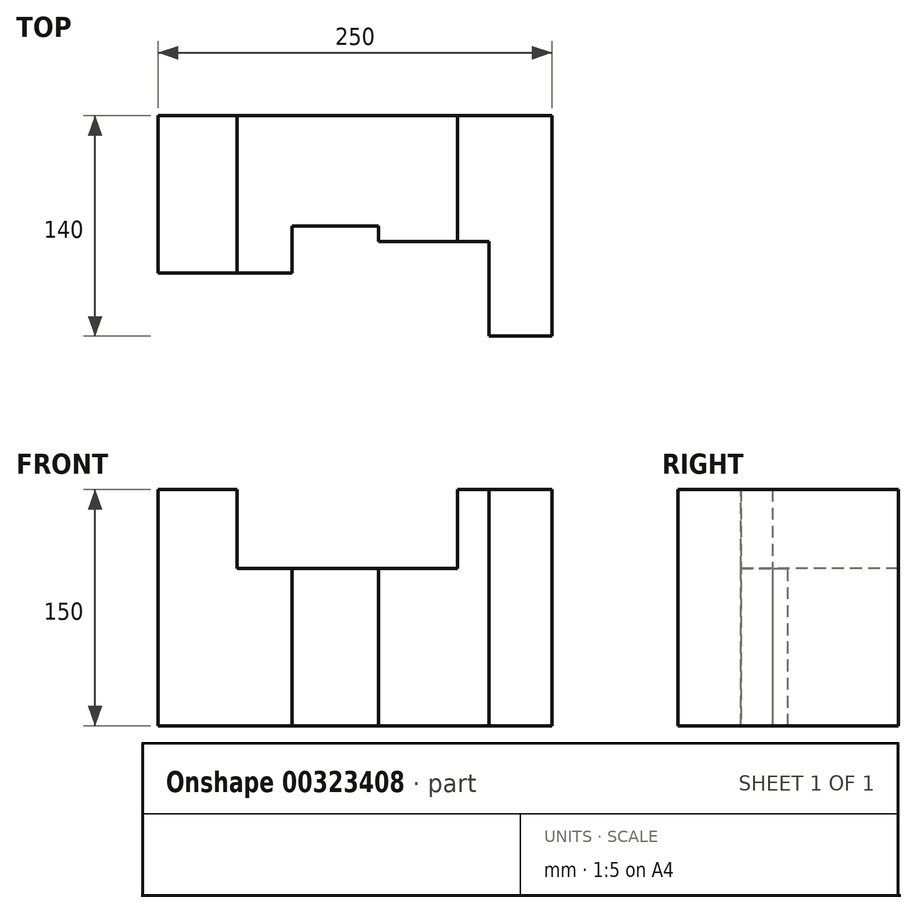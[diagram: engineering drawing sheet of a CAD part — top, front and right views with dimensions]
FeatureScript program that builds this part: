
annotation { "Feature Type Name" : "Feature", "Feature Type Description" : "" }
export const myFeature = defineFeature(function(context is Context, id is Id, definition is map)
    precondition{}
    {
        {
            var Q0;
            Q0=qCreatedBy(makeId("Front.planeOp"),FACE);
            var sketch = newSketch(context, id + "F0", { "sketchPlane" : qUnion([Q0])});
            skLineSegment(sketch, "E0.bottom", {"start": v(0, 0) * mm, "end": v(250, 0) * mm});
            skLineSegment(sketch, "E0.top", {"start": v(0, 150) * mm, "end": v(250, 150) * mm});
            skLineSegment(sketch, "E0.left", {"start": v(0, 0) * mm, "end": v(0, 150) * mm});
            skLineSegment(sketch, "E0.right", {"start": v(250, 0) * mm, "end": v(250, 150) * mm});
            skSolve(sketch);
        }
        {
            var Q0;
            Q0 = qSketchRegion(id + "F0", true);
            extrude(context, id + "F1", {"entities" : qUnion([Q0]), "oppositeDirection" : true, "depth" : 140 * mm});
        }
        {
            var Q0;
            Q0=makeQuery(id+"F1.opExtrude","CAP_FACE",FACE,{"disambiguationData":[OSD([sQuery(id+"F0.wireOp",EDGE,"E0.bottom"),sQuery(id+"F0.wireOp",EDGE,"E0.top"),sQuery(id+"F0.wireOp",EDGE,"E0.left"),sQuery(id+"F0.wireOp",EDGE,"E0.right")])],"isStart":true});
            var sketch = newSketch(context, id + "F2", { "sketchPlane" : qUnion([Q0])});
            skLineSegment(sketch, "E1", {"start": v(0, 150) * mm, "end": v(50, 150) * mm});
            skLineSegment(sketch, "E2.bottom", {"start": v(50, 150) * mm, "end": v(190, 150) * mm});
            skLineSegment(sketch, "E2.top", {"start": v(50, 100) * mm, "end": v(190, 100) * mm});
            skLineSegment(sketch, "E2.left", {"start": v(50, 150) * mm, "end": v(50, 100) * mm});
            skLineSegment(sketch, "E2.right", {"start": v(190, 150) * mm, "end": v(190, 100) * mm});
            skSolve(sketch);
        }
        {
            var Q0;
            Q0 = qSketchRegion(id + "F2", true);
            extrude(context, id + "F3", {"entities" : qUnion([Q0]), "operationType" : NewBodyOperationType.REMOVE, "endBound" : BoundingType.THROUGH_ALL, "oppositeDirection" : true, "depth" : 25 * mm});
        }
        {
            var Q0;
            Q0=makeQuery(id+"F1.opExtrude","SWEPT_FACE",FACE,{"disambiguationData":[OSD([sQuery(id+"F0.wireOp",EDGE,"E0.bottom")])]});
            var sketch = newSketch(context, id + "F4", { "sketchPlane" : qUnion([Q0])});
            skLineSegment(sketch, "E3", {"start": v(250, 0) * mm, "end": v(210, 0) * mm});
            skLineSegment(sketch, "E4.bottom", {"start": v(210, 0) * mm, "end": v(0, 0) * mm});
            skLineSegment(sketch, "E4.top", {"start": v(210, 0) * mm, "end": v(0, 0) * mm});
            skLineSegment(sketch, "E4.left", {"start": v(210, 0) * mm, "end": v(210, 0) * mm});
            skLineSegment(sketch, "E4.right", {"start": v(0, 0) * mm, "end": v(0, 0) * mm});
            skLineSegment(sketch, "E5.top", {"start": v(210, -40) * mm, "end": v(0, -40) * mm});
            skLineSegment(sketch, "E5.left", {"start": v(210, 0) * mm, "end": v(210, -40) * mm});
            skLineSegment(sketch, "E5.right", {"start": v(0, 0) * mm, "end": v(0, -40) * mm});
            skSolve(sketch);
        }
        {
            var Q0;
            Q0 = qSketchRegion(id + "F4", true);
            extrude(context, id + "F5", {"entities" : qUnion([Q0]), "operationType" : NewBodyOperationType.REMOVE, "endBound" : BoundingType.THROUGH_ALL, "oppositeDirection" : true, "depth" : 25 * mm});
        }
        {
            var Q0;
            Q0=makeQuery(id+"F3.boolean.opBoolean","COPY",FACE,{"derivedFrom":makeQuery(id+"F3.opExtrude","SWEPT_FACE",FACE,{"disambiguationData":[OSD([sQuery(id+"F2.wireOp",EDGE,"E2.top")])]})});
            var sketch = newSketch(context, id + "F6", { "sketchPlane" : qUnion([Q0])});
            skLineSegment(sketch, "E6", {"start": v(50, 40) * mm, "end": v(85, 40) * mm});
            skLineSegment(sketch, "E7.bottom", {"start": v(85, 40) * mm, "end": v(140, 40) * mm});
            skLineSegment(sketch, "E7.top", {"start": v(85, 70) * mm, "end": v(140, 70) * mm});
            skLineSegment(sketch, "E7.left", {"start": v(85, 40) * mm, "end": v(85, 70) * mm});
            skLineSegment(sketch, "E7.right", {"start": v(140, 40) * mm, "end": v(140, 70) * mm});
            skSolve(sketch);
        }
        {
            var Q0;
            Q0 = qSketchRegion(id + "F6", true);
            extrude(context, id + "F7", {"entities" : qUnion([Q0]), "operationType" : NewBodyOperationType.REMOVE, "endBound" : BoundingType.THROUGH_ALL, "oppositeDirection" : true, "depth" : 25 * mm});
        }
        {
            var Q0;
            Q0=makeQuery(id+"F1.opExtrude","SWEPT_FACE",FACE,{"disambiguationData":[OSD([sQuery(id+"F0.wireOp",EDGE,"E0.bottom")])]});
            var sketch = newSketch(context, id + "F8", { "sketchPlane" : qUnion([Q0])});
            skLineSegment(sketch, "E8", {"start": v(140, -40) * mm, "end": v(140, -60) * mm});
            skLineSegment(sketch, "E9", {"start": v(140, -60) * mm, "end": v(210, -60) * mm});
            skLineSegment(sketch, "E10", {"start": v(210, -60) * mm, "end": v(210, -40) * mm});
            skLineSegment(sketch, "E11", {"start": v(210, -40) * mm, "end": v(140, -40) * mm});
            skSolve(sketch);
        }
        {
            var Q0;
            Q0 = qSketchRegion(id + "F8", true);
            extrude(context, id + "F9", {"entities" : qUnion([Q0]), "operationType" : NewBodyOperationType.REMOVE, "endBound" : BoundingType.THROUGH_ALL, "oppositeDirection" : true, "depth" : 25 * mm});
        }
    });
